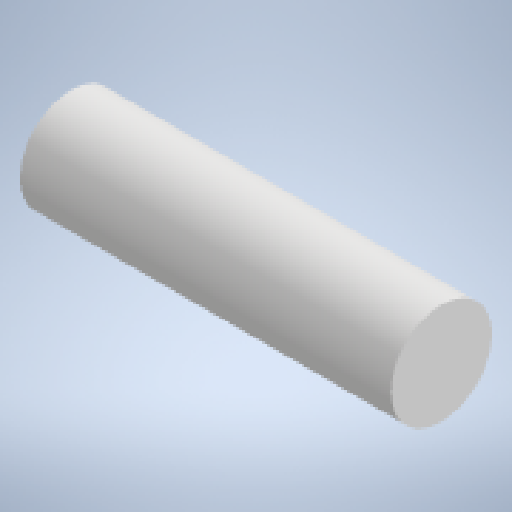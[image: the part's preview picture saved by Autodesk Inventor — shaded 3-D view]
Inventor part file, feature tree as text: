
AUTODESK INVENTOR PART (.ipt)
format: ipt  version: 2025 (Build 290162010, 162A)  size: 141,312 bytes
history: native  units: mm
features: extrude x1, sketch x1
ambient origin geometry x8: Origin, YZ Plane, XZ Plane, XY Plane, X Axis, Y Axis, Z Axis, Center Point
bodies: Volumenkörper1 (feature_tree)
feature tree (2):
  extrude  "Extrusion1"  Depth=55.0mm TaperAngle=0.0deg
  sketch  "Skizze1"  dims[d0=15.0mm d1=55.0mm d2=0.0mm d3=15.0mm d4=15.0mm d5=15.0mm d6=15.0mm]
